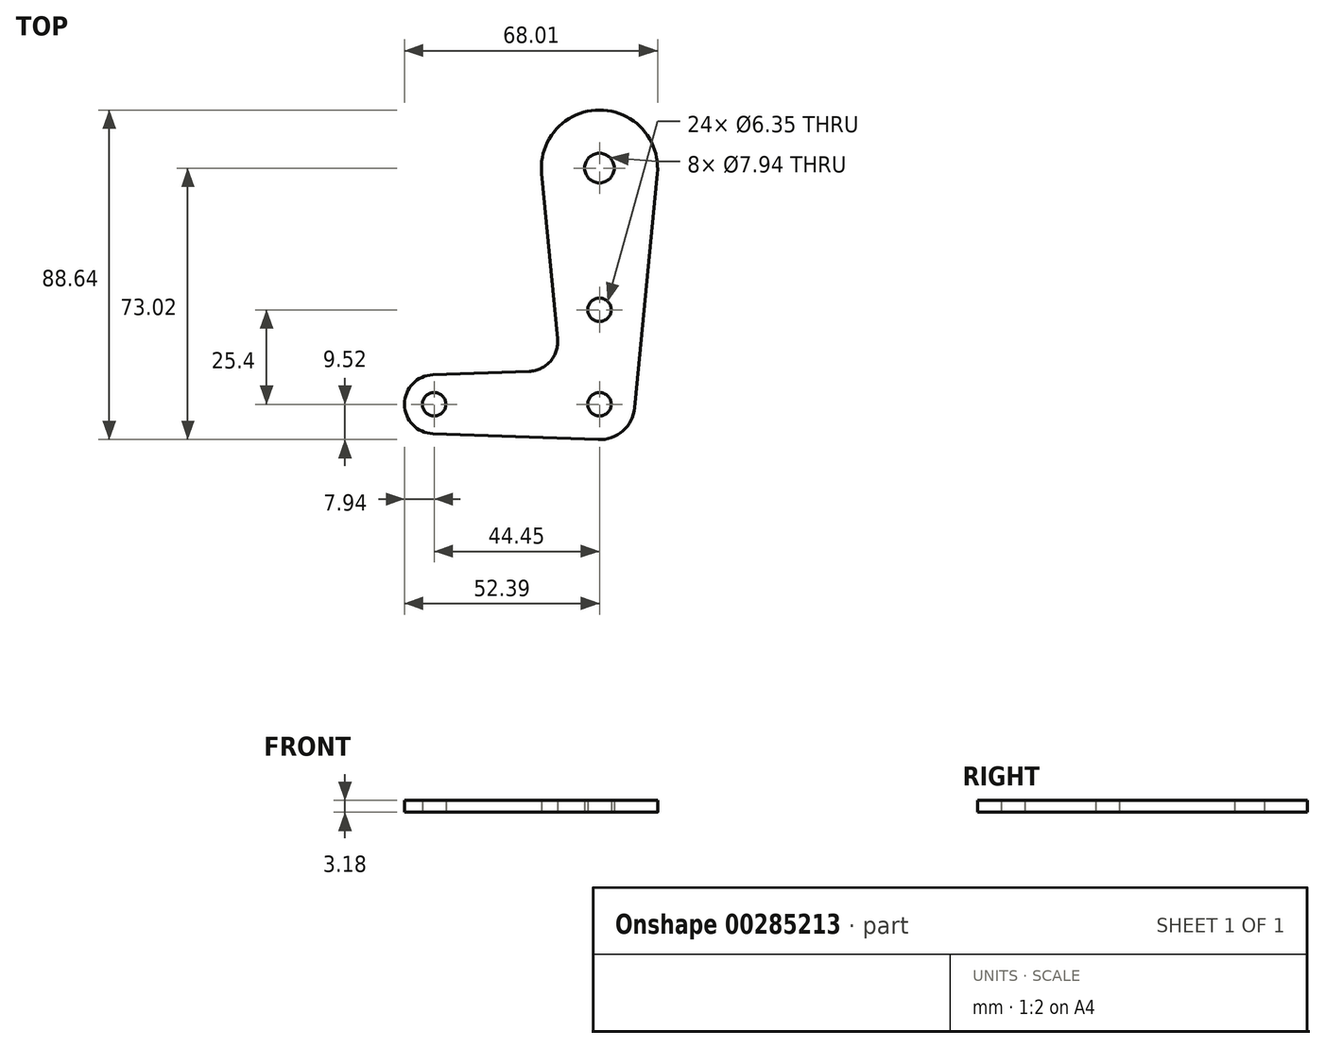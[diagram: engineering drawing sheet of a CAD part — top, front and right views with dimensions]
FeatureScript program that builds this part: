
annotation { "Feature Type Name" : "Feature", "Feature Type Description" : "" }
export const myFeature = defineFeature(function(context is Context, id is Id, definition is map)
    precondition{}
    {
        {
            var Q0;
            Q0=qCreatedBy(makeId("Top.planeOp"),FACE);
            var sketch = newSketch(context, id + "F0", { "sketchPlane" : qUnion([Q0])});
            skCircle(sketch, "E0", {"center": v(0, 0) * mm, "radius": 3.18 * mm});
            skCircle(sketch, "E1", {"center": v(0, 63.5) * mm, "radius": 3.97 * mm});
            skCircle(sketch, "E2", {"center": v(-44.45, 0) * mm, "radius": 3.18 * mm});
            skCircle(sketch, "E3", {"center": v(-44.45, 0) * mm, "radius": 7.94 * mm});
            skCircle(sketch, "E4", {"center": v(0, 0) * mm, "radius": 9.53 * mm});
            skCircle(sketch, "E5", {"center": v(0, 63.5) * mm, "radius": 15.62 * mm});
            skLineSegment(sketch, "E6", {"start": v(-44.73, -7.93) * mm, "end": v(-0.34, -9.52) * mm});
            skLineSegment(sketch, "E7", {"start": v(-44.73, 7.93) * mm, "end": v(-18.88, 8.86) * mm});
            skLineSegment(sketch, "E8", {"start": v(-15.77, 64.25) * mm, "end": v(-11.26, 17.55) * mm});
            skLineSegment(sketch, "E9", {"start": v(15.62, 62.77) * mm, "end": v(9.48, -0.91) * mm});
            skArc(sketch, "E10.filletArc", {"start": v(-18.88, 8.86) * mm, "mid": v(-13.2, 11.56) * mm, "end": v(-11.26, 17.55) * mm});
            skLineSegment(sketch, "E11", {"start": v(0, 63.5) * mm, "end": v(0, 0) * mm, "construction": true});
            skCircle(sketch, "E12", {"center": v(0, 25.4) * mm, "radius": 3.18 * mm});
            skSolve(sketch);
        }
        {
            var Q0;
            Q0 = qSketchRegion(id + "F0", true);
            extrude(context, id + "F1", {"entities" : qUnion([Q0]), "depth" : 3.17 * mm});
        }
    });
